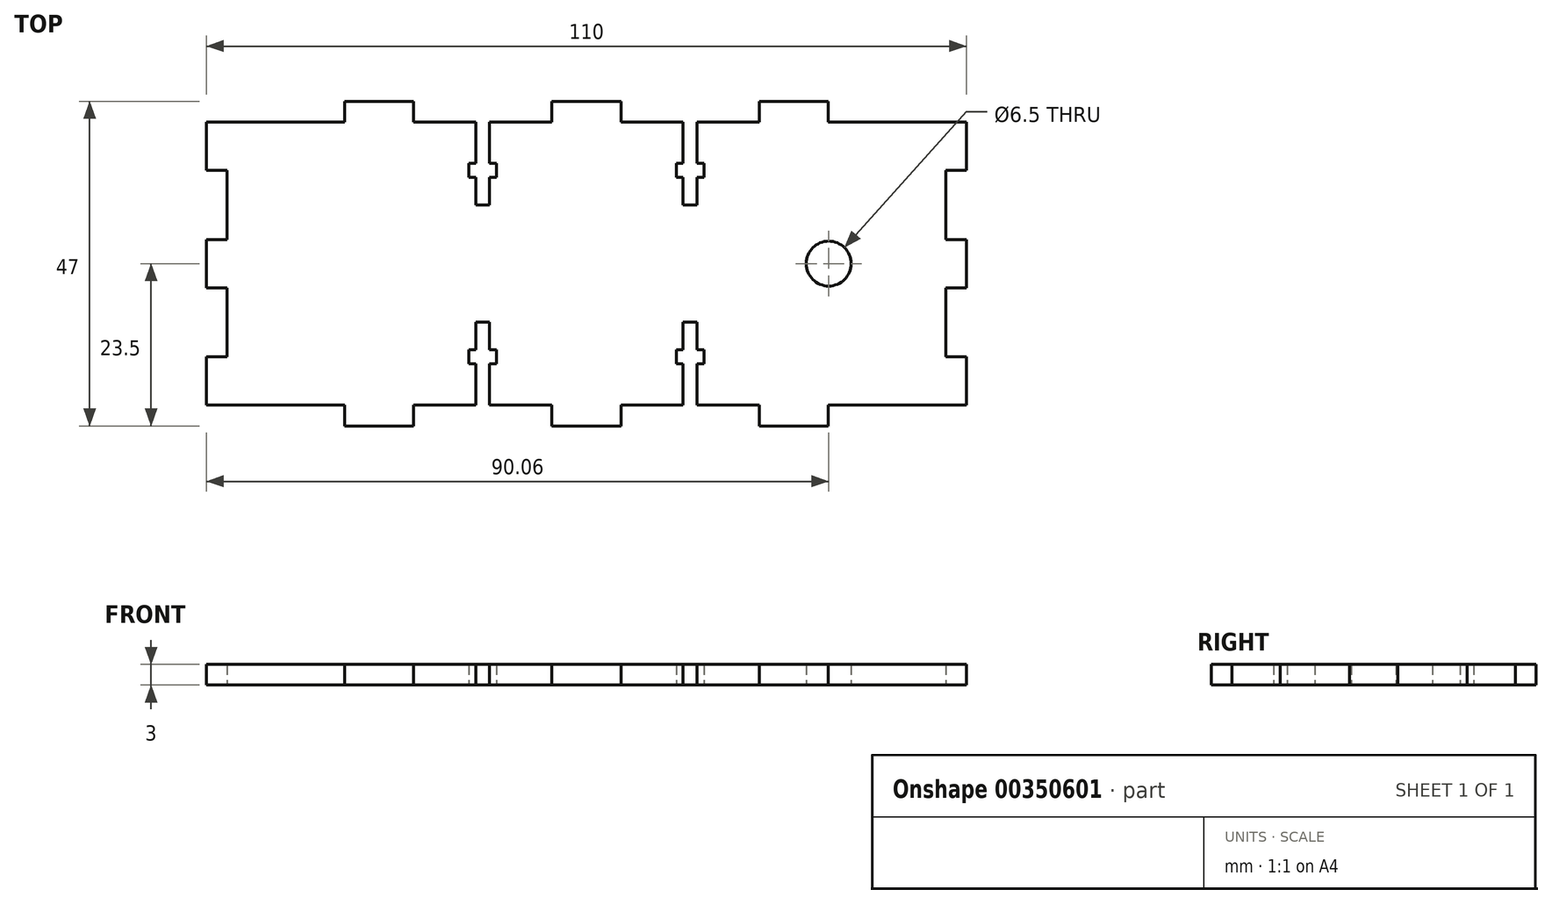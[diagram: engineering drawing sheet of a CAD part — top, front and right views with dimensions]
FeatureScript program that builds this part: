
annotation { "Feature Type Name" : "Feature", "Feature Type Description" : "" }
export const myFeature = defineFeature(function(context is Context, id is Id, definition is map)
    precondition{}
    {
        {
            var Q0;
            Q0=qCreatedBy(makeId("Top.planeOp"),FACE);
            var sketch = newSketch(context, id + "F0", { "sketchPlane" : qUnion([Q0])});
            skLineSegment(sketch, "E0.top", {"start": v(-66.36, 0) * mm, "end": v(-46.36, 0) * mm});
            skLineSegment(sketch, "E0.left", {"start": v(-66.36, 20.5) * mm, "end": v(-66.36, 17) * mm});
            skLineSegment(sketch, "E0.right", {"start": v(43.64, 20.5) * mm, "end": v(43.64, 17) * mm});
            skLineSegment(sketch, "E1", {"start": v(-46.36, 0) * mm, "end": v(-46.36, -3) * mm});
            skLineSegment(sketch, "E2", {"start": v(-46.36, -3) * mm, "end": v(-36.36, -3) * mm});
            skLineSegment(sketch, "E3", {"start": v(-36.36, -3) * mm, "end": v(-36.36, 0) * mm});
            skLineSegment(sketch, "E4", {"start": v(-16.36, 0) * mm, "end": v(-16.36, -3) * mm});
            skLineSegment(sketch, "E5", {"start": v(-16.36, -3) * mm, "end": v(-6.36, -3) * mm});
            skLineSegment(sketch, "E6", {"start": v(-6.36, -3) * mm, "end": v(-6.36, 0) * mm});
            skLineSegment(sketch, "E7", {"start": v(13.64, 0) * mm, "end": v(13.64, -3) * mm});
            skLineSegment(sketch, "E8", {"start": v(13.64, -3) * mm, "end": v(23.64, -3) * mm});
            skLineSegment(sketch, "E9", {"start": v(23.64, -3) * mm, "end": v(23.64, 0) * mm});
            skLineSegment(sketch, "E10.trimOffspring", {"start": v(-36.36, 0) * mm, "end": v(-27.36, 0) * mm});
            skLineSegment(sketch, "E11.trimOffspring", {"start": v(-6.36, 0) * mm, "end": v(2.64, 0) * mm});
            skLineSegment(sketch, "E12.trimOffspring", {"start": v(23.64, 0) * mm, "end": v(43.64, 0) * mm});
            skLineSegment(sketch, "E13", {"start": v(-27.36, 0) * mm, "end": v(-27.36, 6) * mm});
            skLineSegment(sketch, "E14", {"start": v(-25.36, 0) * mm, "end": v(-25.36, 6) * mm});
            skLineSegment(sketch, "E15", {"start": v(-25.36, 6) * mm, "end": v(-24.36, 6) * mm});
            skLineSegment(sketch, "E16", {"start": v(-24.36, 6) * mm, "end": v(-24.36, 8) * mm});
            skLineSegment(sketch, "E17", {"start": v(-24.36, 8) * mm, "end": v(-25.36, 8) * mm});
            skLineSegment(sketch, "E18", {"start": v(-25.36, 8) * mm, "end": v(-25.36, 12) * mm});
            skLineSegment(sketch, "E19", {"start": v(-25.36, 12) * mm, "end": v(-27.36, 12) * mm});
            skLineSegment(sketch, "E20", {"start": v(-27.36, 12) * mm, "end": v(-27.36, 8) * mm});
            skLineSegment(sketch, "E21", {"start": v(-27.36, 8) * mm, "end": v(-28.36, 8) * mm});
            skLineSegment(sketch, "E22", {"start": v(-28.36, 8) * mm, "end": v(-28.36, 6) * mm});
            skLineSegment(sketch, "E23", {"start": v(-28.36, 6) * mm, "end": v(-27.36, 6) * mm});
            skLineSegment(sketch, "E24", {"start": v(2.64, 0) * mm, "end": v(2.64, 6) * mm});
            skLineSegment(sketch, "E25", {"start": v(4.64, 0) * mm, "end": v(4.64, 6) * mm});
            skLineSegment(sketch, "E26", {"start": v(4.64, 6) * mm, "end": v(5.64, 6) * mm});
            skLineSegment(sketch, "E27", {"start": v(5.64, 6) * mm, "end": v(5.64, 8) * mm});
            skLineSegment(sketch, "E28", {"start": v(5.64, 8) * mm, "end": v(4.64, 8) * mm});
            skLineSegment(sketch, "E29", {"start": v(4.64, 8) * mm, "end": v(4.64, 12) * mm});
            skLineSegment(sketch, "E30", {"start": v(4.64, 12) * mm, "end": v(2.64, 12) * mm});
            skLineSegment(sketch, "E31", {"start": v(2.64, 12) * mm, "end": v(2.64, 8) * mm});
            skLineSegment(sketch, "E32", {"start": v(2.64, 8) * mm, "end": v(1.64, 8) * mm});
            skLineSegment(sketch, "E33", {"start": v(1.64, 8) * mm, "end": v(1.64, 6) * mm});
            skLineSegment(sketch, "E34", {"start": v(1.64, 6) * mm, "end": v(2.64, 6) * mm});
            skLineSegment(sketch, "E35", {"start": v(43.64, 7) * mm, "end": v(40.64, 7) * mm});
            skLineSegment(sketch, "E36", {"start": v(40.64, 7) * mm, "end": v(40.64, 17) * mm});
            skLineSegment(sketch, "E37", {"start": v(40.64, 17) * mm, "end": v(43.64, 17) * mm});
            skLineSegment(sketch, "E38.trimOffspring", {"start": v(43.64, 7) * mm, "end": v(43.64, 0) * mm});
            skLineSegment(sketch, "E39.trimOffspring", {"start": v(-66.36, 7) * mm, "end": v(-66.36, 0) * mm});
            skLineSegment(sketch, "E40.MirrorCS", {"start": v(1.64, 35) * mm, "end": v(2.64, 35) * mm});
            skLineSegment(sketch, "E41.MirrorCS", {"start": v(-24.36, 33) * mm, "end": v(-25.36, 33) * mm});
            skLineSegment(sketch, "E42.MirrorCS", {"start": v(1.64, 33) * mm, "end": v(1.64, 35) * mm});
            skLineSegment(sketch, "E43.MirrorCS", {"start": v(4.64, 35) * mm, "end": v(5.64, 35) * mm});
            skLineSegment(sketch, "E44.MirrorCS", {"start": v(2.64, 33) * mm, "end": v(1.64, 33) * mm});
            skLineSegment(sketch, "E45.MirrorCS", {"start": v(-27.36, 33) * mm, "end": v(-28.36, 33) * mm});
            skLineSegment(sketch, "E46.MirrorCS", {"start": v(5.64, 35) * mm, "end": v(5.64, 33) * mm});
            skLineSegment(sketch, "E47.MirrorCS", {"start": v(4.64, 29) * mm, "end": v(2.64, 29) * mm});
            skLineSegment(sketch, "E48.MirrorCS", {"start": v(-28.36, 33) * mm, "end": v(-28.36, 35) * mm});
            skLineSegment(sketch, "E49.MirrorCS", {"start": v(-24.36, 35) * mm, "end": v(-24.36, 33) * mm});
            skLineSegment(sketch, "E50.MirrorCS", {"start": v(-28.36, 35) * mm, "end": v(-27.36, 35) * mm});
            skLineSegment(sketch, "E51.MirrorCS", {"start": v(-25.36, 29) * mm, "end": v(-27.36, 29) * mm});
            skLineSegment(sketch, "E52.MirrorCS", {"start": v(5.64, 33) * mm, "end": v(4.64, 33) * mm});
            skLineSegment(sketch, "E53.MirrorCS", {"start": v(-25.36, 35) * mm, "end": v(-24.36, 35) * mm});
            skLineSegment(sketch, "E54.MirrorCS", {"start": v(-27.36, 29) * mm, "end": v(-27.36, 33) * mm});
            skLineSegment(sketch, "E55.MirrorCS", {"start": v(23.64, 44) * mm, "end": v(23.64, 41) * mm});
            skLineSegment(sketch, "E56.MirrorCS", {"start": v(13.64, 41) * mm, "end": v(13.64, 44) * mm});
            skLineSegment(sketch, "E57.MirrorCS", {"start": v(-6.36, 44) * mm, "end": v(-6.36, 41) * mm});
            skLineSegment(sketch, "E58.MirrorCS", {"start": v(-16.36, 41) * mm, "end": v(-16.36, 44) * mm});
            skLineSegment(sketch, "E59.MirrorCS", {"start": v(-46.36, 41) * mm, "end": v(-46.36, 44) * mm});
            skLineSegment(sketch, "E60.MirrorCS", {"start": v(-36.36, 44) * mm, "end": v(-36.36, 41) * mm});
            skLineSegment(sketch, "E61.MirrorCS", {"start": v(40.64, 24) * mm, "end": v(43.64, 24) * mm});
            skLineSegment(sketch, "E62.MirrorCS", {"start": v(43.64, 34) * mm, "end": v(40.64, 34) * mm});
            skLineSegment(sketch, "E63.MirrorCS", {"start": v(2.64, 29) * mm, "end": v(2.64, 33) * mm});
            skLineSegment(sketch, "E64.MirrorCS", {"start": v(-6.36, 41) * mm, "end": v(2.64, 41) * mm});
            skLineSegment(sketch, "E65.MirrorCS", {"start": v(23.64, 41) * mm, "end": v(43.64, 41) * mm});
            skLineSegment(sketch, "E66.MirrorCS", {"start": v(-66.36, 34) * mm, "end": v(-66.36, 41) * mm});
            skLineSegment(sketch, "E67.MirrorCS", {"start": v(40.64, 34) * mm, "end": v(40.64, 24) * mm});
            skLineSegment(sketch, "E68.MirrorCS", {"start": v(2.64, 41) * mm, "end": v(2.64, 35) * mm});
            skLineSegment(sketch, "E69.MirrorCS", {"start": v(-27.36, 41) * mm, "end": v(-27.36, 35) * mm});
            skLineSegment(sketch, "E70.MirrorCS", {"start": v(13.64, 44) * mm, "end": v(23.64, 44) * mm});
            skLineSegment(sketch, "E71.MirrorCS", {"start": v(-66.36, 41) * mm, "end": v(-46.36, 41) * mm});
            skLineSegment(sketch, "E72.MirrorCS", {"start": v(4.64, 33) * mm, "end": v(4.64, 29) * mm});
            skLineSegment(sketch, "E73.MirrorCS", {"start": v(-16.36, 44) * mm, "end": v(-6.36, 44) * mm});
            skLineSegment(sketch, "E74.MirrorCS", {"start": v(-66.36, 20.5) * mm, "end": v(-66.36, 24) * mm});
            skLineSegment(sketch, "E75.MirrorCS", {"start": v(-36.36, 41) * mm, "end": v(-27.36, 41) * mm});
            skLineSegment(sketch, "E76.MirrorCS", {"start": v(43.64, 20.5) * mm, "end": v(43.64, 24) * mm});
            skLineSegment(sketch, "E77.MirrorCS", {"start": v(-46.36, 44) * mm, "end": v(-36.36, 44) * mm});
            skLineSegment(sketch, "E78.MirrorCS", {"start": v(4.64, 41) * mm, "end": v(4.64, 35) * mm});
            skLineSegment(sketch, "E79.MirrorCS", {"start": v(-25.36, 33) * mm, "end": v(-25.36, 29) * mm});
            skLineSegment(sketch, "E80.MirrorCS", {"start": v(-25.36, 41) * mm, "end": v(-25.36, 35) * mm});
            skLineSegment(sketch, "E81.MirrorCS", {"start": v(43.64, 34) * mm, "end": v(43.64, 41) * mm});
            skLineSegment(sketch, "E82.MirrorCS", {"start": v(-66.36, 7) * mm, "end": v(-63.36, 7) * mm});
            skLineSegment(sketch, "E83.MirrorCS", {"start": v(-63.36, 24) * mm, "end": v(-66.36, 24) * mm});
            skLineSegment(sketch, "E84.MirrorCS", {"start": v(-63.36, 17) * mm, "end": v(-66.36, 17) * mm});
            skLineSegment(sketch, "E85.MirrorCS", {"start": v(-66.36, 34) * mm, "end": v(-63.36, 34) * mm});
            skLineSegment(sketch, "E86.MirrorCS", {"start": v(-63.36, 34) * mm, "end": v(-63.36, 24) * mm});
            skLineSegment(sketch, "E87.MirrorCS", {"start": v(-63.36, 7) * mm, "end": v(-63.36, 17) * mm});
            skCircle(sketch, "E88", {"center": v(23.7, 20.5) * mm, "radius": 3.25 * mm});
            skLineSegment(sketch, "E89.trimOffspring", {"start": v(-25.36, 0) * mm, "end": v(-16.36, 0) * mm});
            skLineSegment(sketch, "E90.trimOffspring", {"start": v(4.64, 0) * mm, "end": v(13.64, 0) * mm});
            skLineSegment(sketch, "E91.trimOffspring", {"start": v(-25.36, 41) * mm, "end": v(-16.36, 41) * mm});
            skLineSegment(sketch, "E92.trimOffspring", {"start": v(4.64, 41) * mm, "end": v(13.64, 41) * mm});
            skSolve(sketch);
        }
        {
            var Q0;
            Q0 = qSketchRegion(id + "F0", true);
            extrude(context, id + "F1", {"entities" : qUnion([Q0]), "endBound" : BoundingType.SYMMETRIC, "depth" : 3 * mm});
        }
    });
